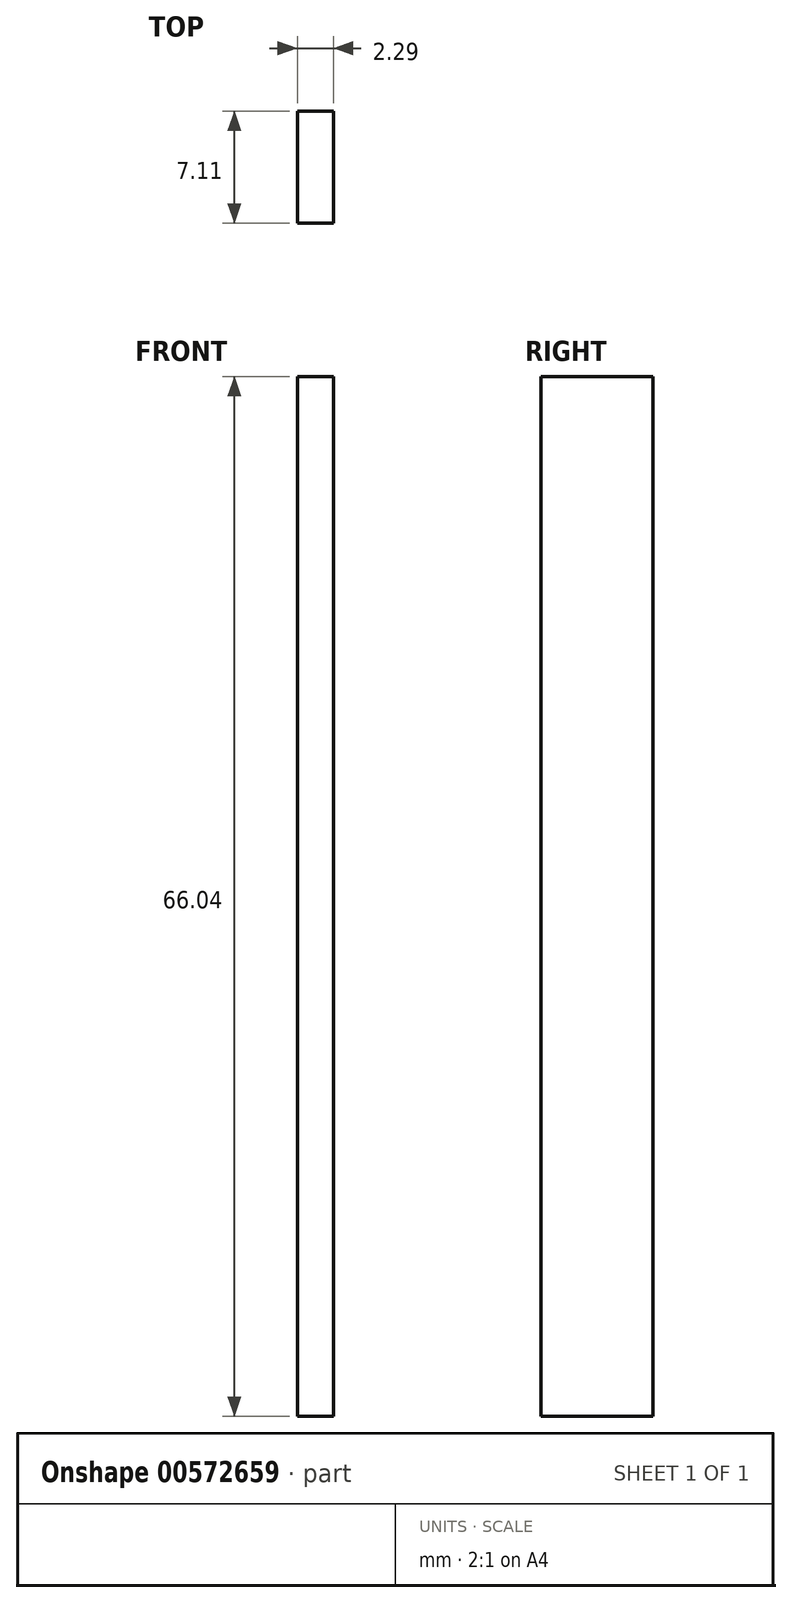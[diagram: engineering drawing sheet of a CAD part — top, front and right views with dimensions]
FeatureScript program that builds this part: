
annotation { "Feature Type Name" : "Feature", "Feature Type Description" : "" }
export const myFeature = defineFeature(function(context is Context, id is Id, definition is map)
    precondition{}
    {
        {
            var Q0;
            Q0=qCreatedBy(makeId("Top.planeOp"),FACE);
            var sketch = newSketch(context, id + "F0", { "sketchPlane" : qUnion([Q0])});
            skLineSegment(sketch, "E0.bottom", {"start": v(-2.29, 7.11) * mm, "end": v(0, 7.11) * mm});
            skLineSegment(sketch, "E0.top", {"start": v(-2.29, 0) * mm, "end": v(0, 0) * mm});
            skLineSegment(sketch, "E0.left", {"start": v(-2.29, 7.11) * mm, "end": v(-2.29, 0) * mm});
            skLineSegment(sketch, "E0.right", {"start": v(0, 7.11) * mm, "end": v(0, 0) * mm});
            skSolve(sketch);
        }
        {
            var Q0;
            Q0=makeQuery(id+"F0.imprint","IMPRINT",FACE,{"disambiguationData":[TD([[makeQuery(id+"F0.imprint","IMPRINT",EDGE,{"derivedFrom":sQuery(id+"F0.wireOp",EDGE,"E0.bottom")}),-1.0]])]});
            extrude(context, id + "F1", {"entities" : qUnion([Q0]), "depth" : 66.04 * mm, "offsetDistance" : 25.4 * mm});
        }
    });
